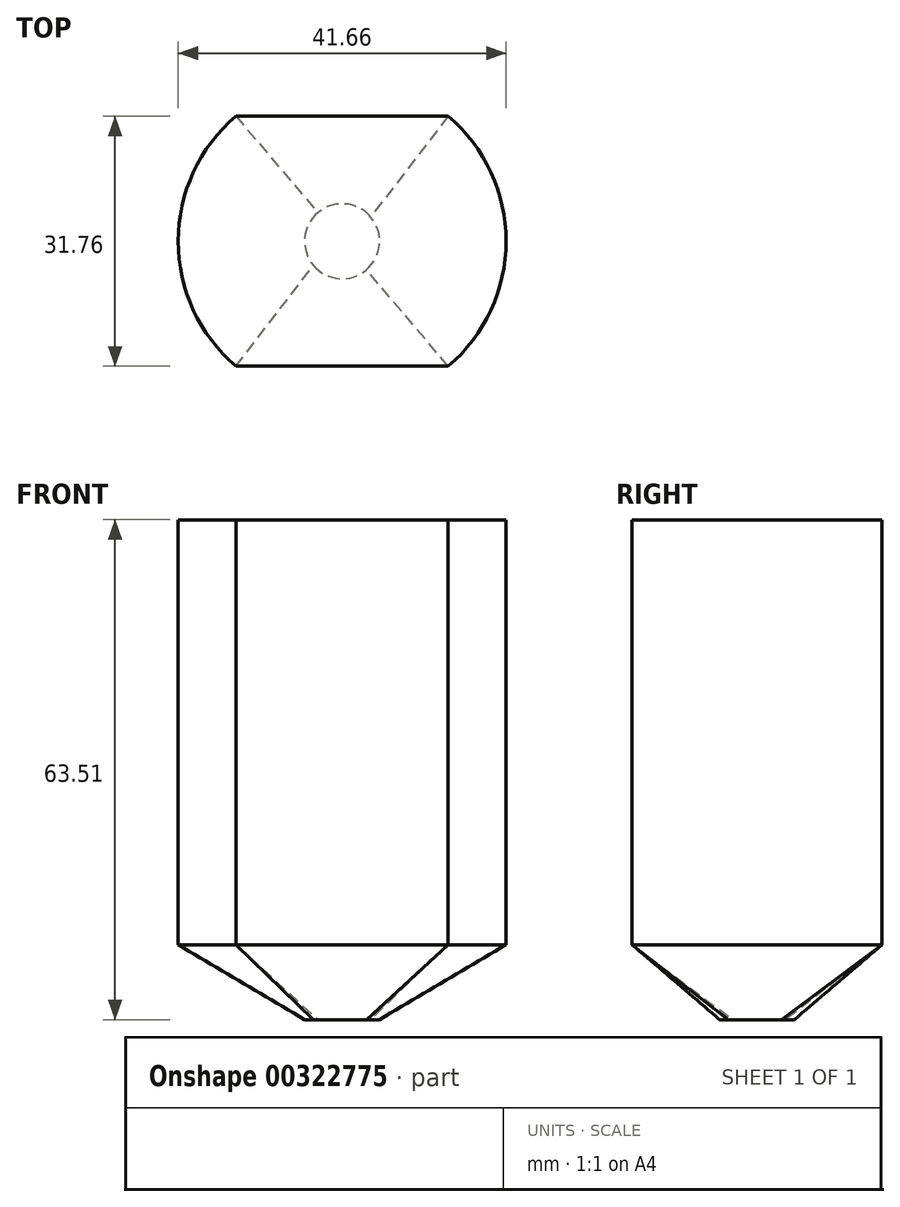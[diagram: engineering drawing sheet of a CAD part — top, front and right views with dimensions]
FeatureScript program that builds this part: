
annotation { "Feature Type Name" : "Feature", "Feature Type Description" : "" }
export const myFeature = defineFeature(function(context is Context, id is Id, definition is map)
    precondition{}
    {
        {
            var Q0;
            Q0=qCreatedBy(makeId("Top.planeOp"),FACE);
            var sketch = newSketch(context, id + "F0", { "sketchPlane" : qUnion([Q0])});
            skArc(sketch, "E0", {"start": v(-13.48, 15.87) * mm, "mid": v(-20.83, 0) * mm, "end": v(-13.48, -15.87) * mm});
            skLineSegment(sketch, "E1", {"start": v(-13.48, 15.88) * mm, "end": v(13.48, 15.88) * mm});
            skLineSegment(sketch, "E2", {"start": v(-13.48, -15.87) * mm, "end": v(13.48, -15.87) * mm});
            skLineSegment(sketch, "E3", {"start": v(0, 0) * mm, "end": v(-9.7, 0) * mm});
            skArc(sketch, "E4.trimOffspring", {"start": v(13.48, -15.87) * mm, "mid": v(20.83, 0) * mm, "end": v(13.48, 15.87) * mm});
            skSolve(sketch);
        }
        {
            var Q0;
            Q0 = qSketchRegion(id + "F0", true);
            extrude(context, id + "F1", {"entities" : qUnion([Q0]), "depth" : 53.97 * mm});
        }
        {
            var Q0;
            Q0=makeQuery(id+"F1.opExtrude","CAP_FACE",FACE,{"disambiguationData":[OSD([sQuery(id+"F0.wireOp",EDGE,"E0"),sQuery(id+"F0.wireOp",EDGE,"E1"),sQuery(id+"F0.wireOp",EDGE,"E2"),sQuery(id+"F0.wireOp",EDGE,"E4.trimOffspring")])],"isStart":true});
            cPlane(context, id + "F2", {"entities" : qUnion([Q0]), "cplaneType" : CPlaneType.OFFSET, "offset" : 9.52 * mm, "width" : 152.4 * mm, "height" : 152.4 * mm});
        }
        {
            var Q0;
            Q0=qCreatedBy(id+"F2.planeOp",FACE);
            var sketch = newSketch(context, id + "F3", { "sketchPlane" : qUnion([Q0])});
            skCircle(sketch, "E5", {"center": v(0, 0) * mm, "radius": 4.76 * mm});
            skSolve(sketch);
        }
        {
            var Q1;
            Q1=makeQuery(id+"F1.opExtrude","CAP_FACE",FACE,{"disambiguationData":[OSD([sQuery(id+"F0.wireOp",EDGE,"E0"),sQuery(id+"F0.wireOp",EDGE,"E1"),sQuery(id+"F0.wireOp",EDGE,"E2"),sQuery(id+"F0.wireOp",EDGE,"E4.trimOffspring")])],"isStart":true});
            var Q2;
            Q2=makeQuery(id+"F3.imprint","IMPRINT",FACE,{"disambiguationData":[TD([[makeQuery(id+"F3.imprint","IMPRINT",EDGE,{"derivedFrom":sQuery(id+"F3.wireOp",EDGE,"E5")}),1.0]])]});
            loft(context, id + "F4", {"operationType" : NewBodyOperationType.ADD, "sheetProfilesArray" : [{ "sheetProfileEntities" : qUnion([Q1]) }, { "sheetProfileEntities" : qUnion([Q2]) }]});
        }
    });
